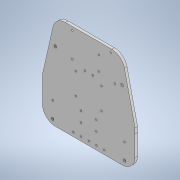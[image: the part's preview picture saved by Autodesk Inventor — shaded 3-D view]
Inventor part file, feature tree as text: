
AUTODESK INVENTOR PART (.ipt)
format: ipt  version: 2020 (Build 240168000, 168)  size: 217,600 bytes
history: native  units: in
note: dims shown in document units (in); Inventor stores cm internally (conversion verified against a paired STEP export)
features: imported_body x1, extrude x1, fillet x1
ambient origin geometry x8: Origin, YZ Plane, XZ Plane, XY Plane, X Axis, Y Axis, Z Axis, Center Point
bodies: Solid1 (feature_tree)
feature tree (3):
  imported_body  "Base"
  extrude  "Extrusion1"  Depth=0.1969in TaperAngle=0.0deg
  fillet  "Fillet1"  Radius=0.9843in
